FCSTD DOCUMENT  (FreeCAD 0.20R29410 (Git))
Label: prancha-editavel-A0-modelo
License: All rights reserved
objects: Sketcher::SketchObject×1
note: 1 computed .brp shape members not serialized (recipe doc carries the construction recipe); baked Part::Feature solids carry a one-line shape summary decoded from their .brp

FEATURE [Sketcher::SketchObject] Sketch
  FullyConstrained = false
  sketch-geometry (12):
    g0: LineSegment StartX=404.816 StartY=599.612 StartZ=0 EndX=-784.184 EndY=599.612 EndZ=0
    g1: LineSegment StartX=-784.184 StartY=599.612 StartZ=0 EndX=-784.184 EndY=-241.388 EndZ=0
    g2: LineSegment StartX=-784.184 StartY=-241.388 StartZ=0 EndX=404.816 EndY=-241.388 EndZ=0
    g3: LineSegment StartX=404.816 StartY=-241.388 StartZ=0 EndX=404.816 EndY=599.612 EndZ=0
    g4: LineSegment StartX=214.816 StartY=-65.4075 StartZ=0 EndX=394.816 EndY=-65.4075 EndZ=0
    g5: LineSegment StartX=394.816 StartY=-65.4075 StartZ=0 EndX=394.816 EndY=-231.388 EndZ=0
    g6: LineSegment StartX=394.816 StartY=-231.388 StartZ=0 EndX=214.816 EndY=-231.388 EndZ=0
    g7: LineSegment StartX=214.816 StartY=-231.388 StartZ=0 EndX=214.816 EndY=-65.4075 EndZ=0
    g8: LineSegment StartX=-764.184 StartY=589.612 StartZ=0 EndX=394.816 EndY=589.612 EndZ=0
    g9: LineSegment StartX=394.816 StartY=589.612 StartZ=0 EndX=394.816 EndY=-231.388 EndZ=0
    g10: LineSegment StartX=394.816 StartY=-231.388 StartZ=0 EndX=-764.184 EndY=-231.388 EndZ=0
    g11: LineSegment StartX=-764.184 StartY=-231.388 StartZ=0 EndX=-764.184 EndY=589.612 EndZ=0
  constraints (33):
    c: Coincident(g0,g1)
    c: Coincident(g1,g2)
    c: Coincident(g2,g3)
    c: Coincident(g3,g0)
    c: Horizontal(g0)
    c: Horizontal(g2)
    c: Vertical(g1)
    c: Vertical(g3)
    c: DistanceX(g0,g0) = 1189
    c: DistanceY(g1,g0) = 841
    c: Coincident(g4,g5)
    c: Coincident(g5,g6)
    c: Coincident(g6,g7)
    c: Coincident(g7,g4)
    c: Horizontal(g4)
    c: Horizontal(g6)
    c: Vertical(g5)
    c: Vertical(g7)
    c: DistanceX(g4,g4) = 180
    c: DistanceX(g5,g2) = 10
    c: DistanceY(g2,g6) = 10
    c: Coincident(g8,g9)
    c: Coincident(g9,g10)
    c: Coincident(g10,g11)
    c: Coincident(g11,g8)
    c: Horizontal(g8)
    c: Horizontal(g10)
    c: Vertical(g9)
    c: Vertical(g11)
    c: DistanceX(g0,g8) = 20
    c: DistanceX(g8,g0) = 10
    c: DistanceY(g8,g0) = 10
    c: DistanceY(g1,g10) = 10
